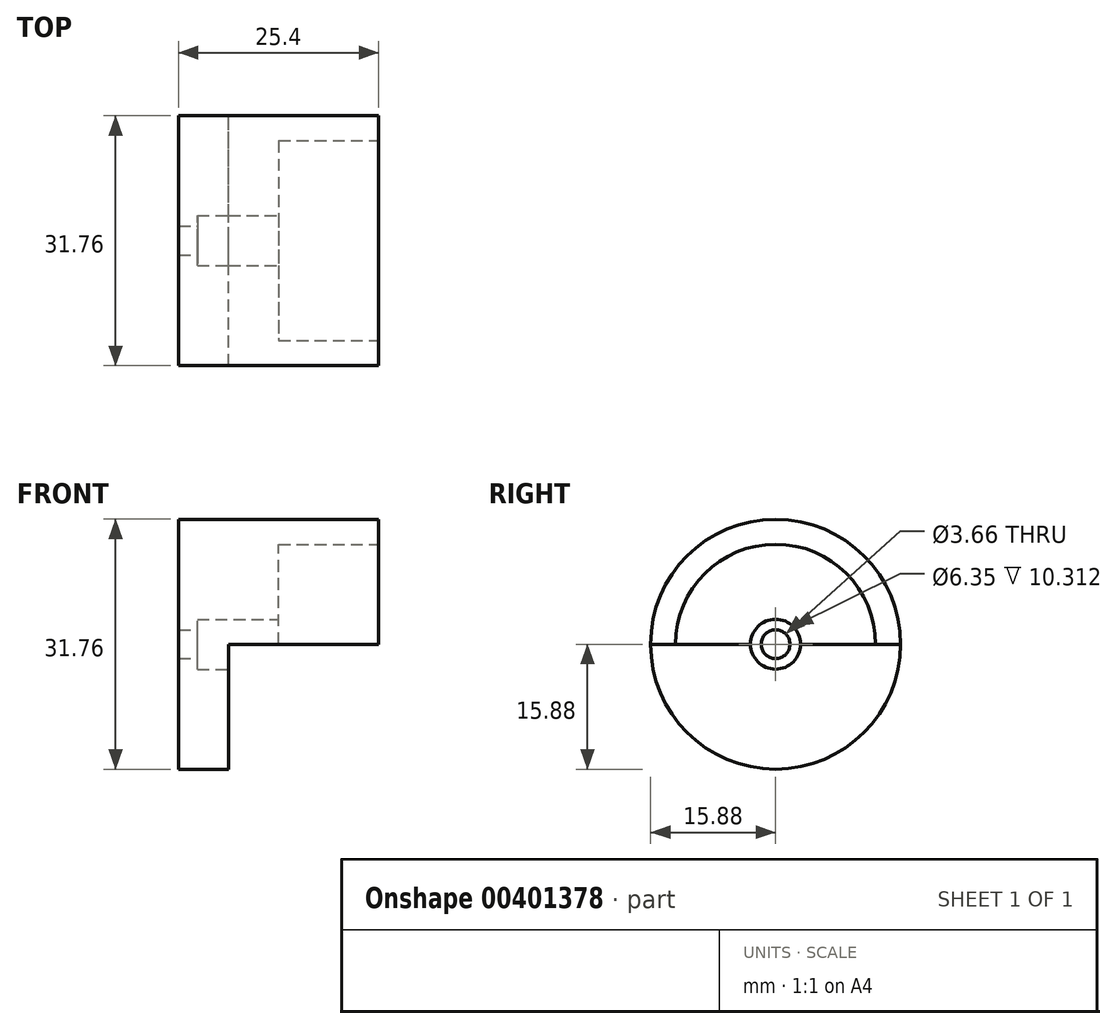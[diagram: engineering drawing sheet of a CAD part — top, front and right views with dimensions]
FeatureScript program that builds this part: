
annotation { "Feature Type Name" : "Feature", "Feature Type Description" : "" }
export const myFeature = defineFeature(function(context is Context, id is Id, definition is map)
    precondition{}
    {
        {
            var Q0;
            Q0=qCreatedBy(makeId("Right.planeOp"),FACE);
            var sketch = newSketch(context, id + "F0", { "sketchPlane" : qUnion([Q0])});
            skCircle(sketch, "E0", {"center": v(0, 0) * mm, "radius": 15.88 * mm});
            skSolve(sketch);
        }
        {
            var Q0;
            Q0=qSketchRegion(id+"F0",true);
            extrude(context, id + "F1", {"entities" : qUnion([Q0]), "depth" : 25.4 * mm});
        }
        {
            var Q0;
            Q0=makeQuery(id+"F1.opExtrude","CAP_FACE",FACE,{"disambiguationData":[OSD([sQuery(id+"F0.wireOp",EDGE,"E0")])],"isStart":false});
            var sketch = newSketch(context, id + "F2", { "sketchPlane" : qUnion([Q0])});
            skLineSegment(sketch, "E1.bottom", {"start": v(-21.15, 0) * mm, "end": v(21.95, 0) * mm});
            skLineSegment(sketch, "E1.top", {"start": v(-21.15, -19.03) * mm, "end": v(21.95, -19.03) * mm});
            skLineSegment(sketch, "E1.left", {"start": v(-21.15, 0) * mm, "end": v(-21.15, -19.03) * mm});
            skLineSegment(sketch, "E1.right", {"start": v(21.95, 0) * mm, "end": v(21.95, -19.03) * mm});
            skSolve(sketch);
        }
        {
            var Q0;
            Q0=qSketchRegion(id+"F2",true);
            extrude(context, id + "F3", {"entities" : qUnion([Q0]), "operationType" : NewBodyOperationType.REMOVE, "oppositeDirection" : true, "depth" : 19.05 * mm});
        }
        {
            var Q0;
            Q0=makeQuery(id+"F3.boolean.opBoolean","COPY",FACE,{"derivedFrom":makeQuery(id+"F3.opExtrude","CAP_FACE",FACE,{"disambiguationData":[OSD([sQuery(id+"F2.wireOp",EDGE,"cWDqX1qf-G7mn-1U2l-sQfb-lu73WZ1OTyqZ"),sQuery(id+"F2.wireOp",EDGE,"E1.bottom"),sQuery(id+"F2.wireOp",EDGE,"E1.top"),sQuery(id+"F2.wireOp",EDGE,"E1.left"),sQuery(id+"F2.wireOp",EDGE,"E1.right")])],"isStart":false})});
            var sketch = newSketch(context, id + "F4", { "sketchPlane" : qUnion([Q0])});
            skCircle(sketch, "E2", {"center": v(0, 0) * mm, "radius": 1.83 * mm});
            skSolve(sketch);
        }
        {
            var Q0;
            Q0=qSketchRegion(id+"F4",true);
            extrude(context, id + "F5", {"entities" : qUnion([Q0]), "operationType" : NewBodyOperationType.REMOVE, "endBound" : BoundingType.THROUGH_ALL, "oppositeDirection" : true, "depth" : 25.4 * mm});
        }
        {
            var Q0;
            Q0=makeQuery(id+"F1.opExtrude","CAP_FACE",FACE,{"disambiguationData":[OSD([sQuery(id+"F0.wireOp",EDGE,"E0")])],"isStart":false});
            var sketch = newSketch(context, id + "F6", { "sketchPlane" : qUnion([Q0])});
            skCircle(sketch, "E3", {"center": v(0, 0) * mm, "radius": 12.7 * mm});
            skSolve(sketch);
        }
        {
            var Q0;
            Q0=qSketchRegion(id+"F6",true);
            extrude(context, id + "F7", {"entities" : qUnion([Q0]), "operationType" : NewBodyOperationType.REMOVE, "oppositeDirection" : true, "depth" : 12.7 * mm});
        }
        {
            var Q0;
            Q0=makeQuery(id+"F1.opExtrude","CAP_FACE",FACE,{"disambiguationData":[OSD([sQuery(id+"F0.wireOp",EDGE,"E0")])],"isStart":false});
            var sketch = newSketch(context, id + "F8", { "sketchPlane" : qUnion([Q0])});
            skCircle(sketch, "E4", {"center": v(0, 0) * mm, "radius": 3.18 * mm});
            skSolve(sketch);
        }
        {
            var Q0;
            Q0=qSketchRegion(id+"F8",true);
            extrude(context, id + "F9", {"entities" : qUnion([Q0]), "operationType" : NewBodyOperationType.REMOVE, "oppositeDirection" : true, "depth" : 23.01 * mm});
        }
    });
